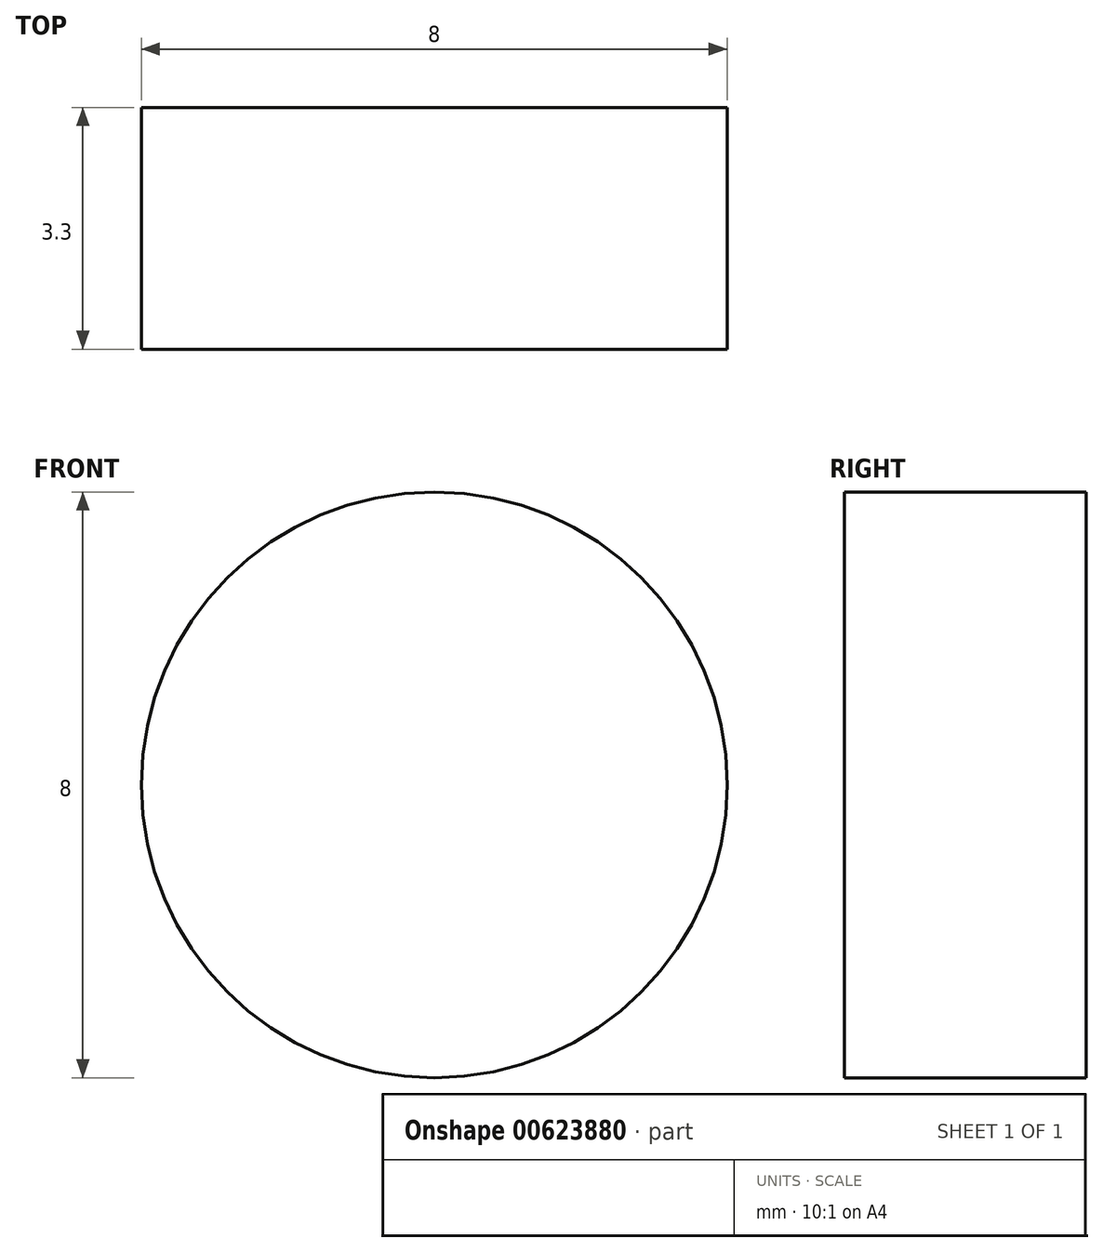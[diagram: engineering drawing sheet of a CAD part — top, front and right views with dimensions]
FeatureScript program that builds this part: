
annotation { "Feature Type Name" : "Feature", "Feature Type Description" : "" }
export const myFeature = defineFeature(function(context is Context, id is Id, definition is map)
    precondition{}
    {
        {
            var Q0;
            Q0=qCreatedBy(makeId("Front.planeOp"),FACE);
            var sketch = newSketch(context, id + "F0", { "sketchPlane" : qUnion([Q0])});
            skCircle(sketch, "E0", {"center": v(0, 0) * mm, "radius": 4 * mm});
            skSolve(sketch);
        }
        {
            var Q0;
            Q0 = qSketchRegion(id + "F0", true);
            extrude(context, id + "F1", {"entities" : qUnion([Q0]), "depth" : 3.3 * mm, "offsetDistance" : 25 * mm});
        }
    });
